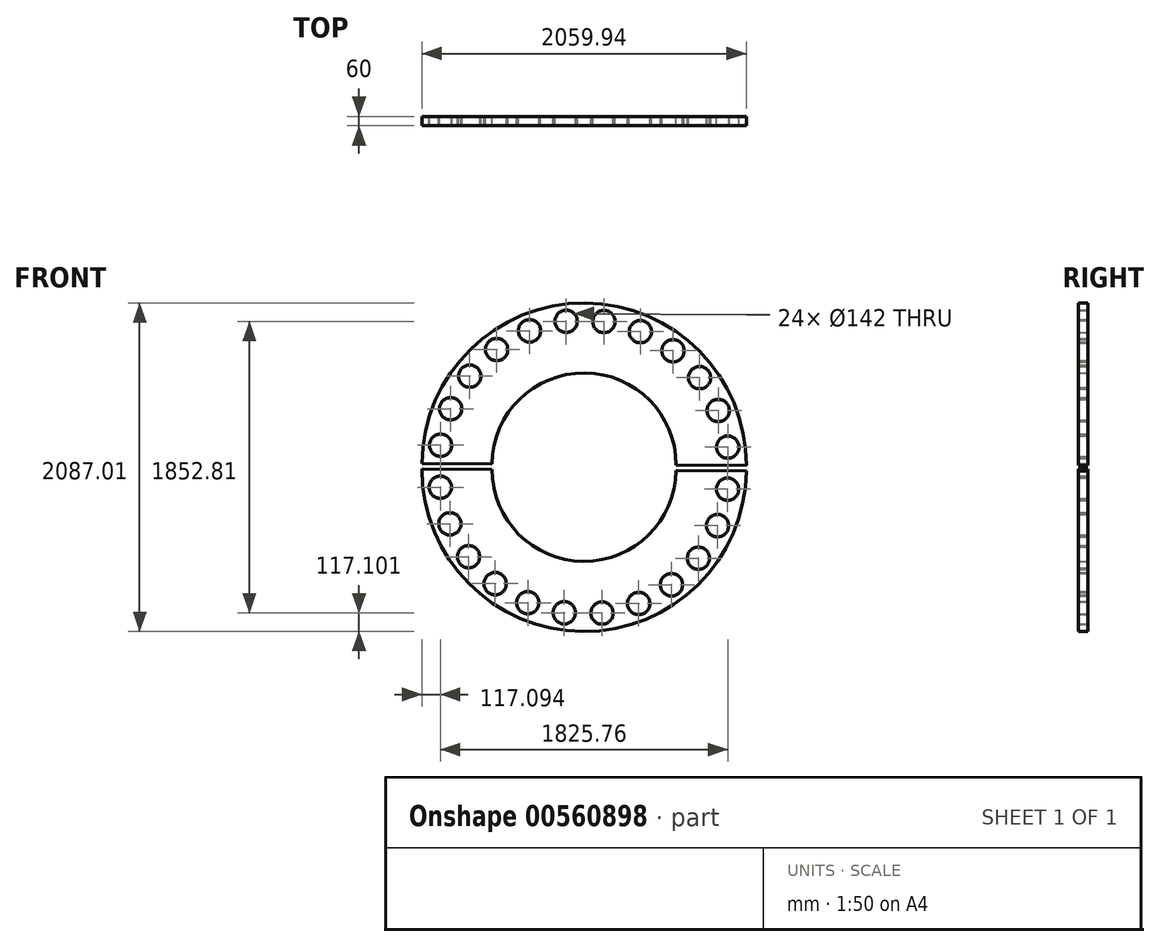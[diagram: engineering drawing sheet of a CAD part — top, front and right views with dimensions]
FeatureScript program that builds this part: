
annotation { "Feature Type Name" : "Feature", "Feature Type Description" : "" }
export const myFeature = defineFeature(function(context is Context, id is Id, definition is map)
    precondition{}
    {
        {
            var Q0;
            Q0=qCreatedBy(makeId("Front.planeOp"),FACE);
            var sketch = newSketch(context, id + "F0", { "sketchPlane" : qUnion([Q0])});
            skLineSegment(sketch, "E0", {"start": v(901.46, 10.69) * mm, "end": v(456.46, 13.63) * mm});
            skLineSegment(sketch, "E1", {"start": v(901.46, -24.31) * mm, "end": v(456.46, -21.37) * mm});
            skLineSegment(sketch, "E2", {"start": v(2071.4, 2.94) * mm, "end": v(2516.4, 0) * mm});
            skLineSegment(sketch, "E3", {"start": v(2071.4, -32.06) * mm, "end": v(2516.4, -35) * mm});
            skArc(sketch, "E4", {"start": v(456.46, 13.63) * mm, "mid": v(1493.22, 1032.8) * mm, "end": v(2516.4, 0) * mm});
            skArc(sketch, "E5", {"start": v(456.46, -21.37) * mm, "mid": v(1479.64, -1054.16) * mm, "end": v(2516.4, -35) * mm});
            skArc(sketch, "E6", {"start": v(901.46, -24.31) * mm, "mid": v(1482.59, -609.17) * mm, "end": v(2071.4, -32.06) * mm});
            skArc(sketch, "E7", {"start": v(901.46, 10.69) * mm, "mid": v(1490.28, 587.8) * mm, "end": v(2071.4, 2.94) * mm});
            skLineSegment(sketch, "E8", {"start": v(456.46, 13.63) * mm, "end": v(456.23, -21.37) * mm, "construction": true});
            skLineSegment(sketch, "E9", {"start": v(2516.4, -35) * mm, "end": v(2516.63, 0) * mm, "construction": true});
            skArc(sketch, "E10", {"start": v(566.46, 12.9) * mm, "mid": v(1492.5, 922.8) * mm, "end": v(2406.4, 0.73) * mm, "construction": true});
            skLineSegment(sketch, "E11", {"start": v(1486.4, 2.82) * mm, "end": v(575.1, 128.93) * mm, "construction": true});
            skCircle(sketch, "E12", {"center": v(575.1, 128.93) * mm, "radius": 71 * mm});
            skLineSegment(sketch, "E13", {"start": v(1486.4, 2.82) * mm, "end": v(1169.22, 4.91) * mm, "construction": true});
            skCircle(sketch, "E14.1.0", {"center": v(638.78, 360.5) * mm, "radius": 71 * mm});
            skCircle(sketch, "E14.2.0", {"center": v(760.24, 567.7) * mm, "radius": 71 * mm});
            skCircle(sketch, "E14.3.0", {"center": v(931.19, 736.4) * mm, "radius": 71 * mm});
            skCircle(sketch, "E14.4.0", {"center": v(1139.97, 855.1) * mm, "radius": 71 * mm});
            skCircle(sketch, "E14.5.0", {"center": v(1372.36, 915.72) * mm, "radius": 71 * mm});
            skCircle(sketch, "E14.6.0", {"center": v(1612.52, 914.13) * mm, "radius": 71 * mm});
            skCircle(sketch, "E14.7.0", {"center": v(1844.1, 850.44) * mm, "radius": 71 * mm});
            skCircle(sketch, "E14.8.0", {"center": v(2051.28, 728.98) * mm, "radius": 71 * mm});
            skCircle(sketch, "E14.9.0", {"center": v(2219.98, 558.03) * mm, "radius": 71 * mm});
            skCircle(sketch, "E14.10.0", {"center": v(2338.69, 349.25) * mm, "radius": 71 * mm});
            skCircle(sketch, "E14.11.0", {"center": v(2399.3, 116.86) * mm, "radius": 71 * mm});
            skLineSegment(sketch, "E14.anchor2", {"start": v(1486.4, 2.82) * mm, "end": v(2399.3, 116.86) * mm, "construction": true});
            skArc(sketch, "E15", {"start": v(566.46, -22.1) * mm, "mid": v(1480.37, -944.17) * mm, "end": v(2406.4, -34.27) * mm, "construction": true});
            skLineSegment(sketch, "E16", {"start": v(1486.46, -24.19) * mm, "end": v(2081.96, -28.13) * mm, "construction": true});
            skLineSegment(sketch, "E17", {"start": v(1486.46, -24.19) * mm, "end": v(2397.77, -150.3) * mm, "construction": true});
            skCircle(sketch, "E18", {"center": v(2397.77, -150.3) * mm, "radius": 71 * mm});
            skCircle(sketch, "E19.1.0", {"center": v(2334.08, -381.87) * mm, "radius": 71 * mm});
            skCircle(sketch, "E19.2.0", {"center": v(2212.62, -589.06) * mm, "radius": 71 * mm});
            skCircle(sketch, "E19.3.0", {"center": v(2041.68, -757.76) * mm, "radius": 71 * mm});
            skCircle(sketch, "E19.4.0", {"center": v(1832.9, -876.47) * mm, "radius": 71 * mm});
            skCircle(sketch, "E19.5.0", {"center": v(1600.5, -937.09) * mm, "radius": 71 * mm});
            skCircle(sketch, "E19.6.0", {"center": v(1360.34, -935.5) * mm, "radius": 71 * mm});
            skCircle(sketch, "E19.7.0", {"center": v(1128.77, -871.8) * mm, "radius": 71 * mm});
            skCircle(sketch, "E19.8.0", {"center": v(921.58, -750.35) * mm, "radius": 71 * mm});
            skCircle(sketch, "E19.9.0", {"center": v(752.88, -579.4) * mm, "radius": 71 * mm});
            skCircle(sketch, "E19.10.0", {"center": v(634.18, -370.62) * mm, "radius": 71 * mm});
            skCircle(sketch, "E19.11.0", {"center": v(573.55, -138.23) * mm, "radius": 71 * mm});
            skLineSegment(sketch, "E19.anchor2", {"start": v(1486.46, -24.19) * mm, "end": v(573.55, -138.23) * mm, "construction": true});
            skLineSegment(sketch, "E20", {"start": v(324.78, -138.23) * mm, "end": v(-1808.55, 249.71) * mm});
            skLineSegment(sketch, "E21", {"start": v(-1808.55, 249.71) * mm, "end": v(365.65, 411.39) * mm});
            skLineSegment(sketch, "E22", {"start": v(365.65, 411.39) * mm, "end": v(324.78, -138.23) * mm});
            skLineSegment(sketch, "E23", {"start": v(1991.2, 1056.17) * mm, "end": v(2514.38, 698.66) * mm});
            skLineSegment(sketch, "E24", {"start": v(2514.38, 698.66) * mm, "end": v(3334.02, 2259.48) * mm});
            skLineSegment(sketch, "E25", {"start": v(3334.02, 2259.48) * mm, "end": v(1991.2, 1056.17) * mm});
            skLineSegment(sketch, "E26", {"start": v(2204.96, -991.46) * mm, "end": v(2566.2, -534.66) * mm});
            skLineSegment(sketch, "E27", {"start": v(2566.2, -534.66) * mm, "end": v(3635.4, -2088.95) * mm});
            skLineSegment(sketch, "E28", {"start": v(3635.4, -2088.95) * mm, "end": v(2204.96, -991.46) * mm});
            skSolve(sketch);
        }
        {
            var Q0;
            Q0=makeQuery(id+"F0.imprint","IMPRINT",FACE,{"disambiguationData":[TD([[makeQuery(id+"F0.imprint","IMPRINT",EDGE,{"derivedFrom":sQuery(id+"F0.wireOp",EDGE,"E0")}),-1.0]])]});
            var Q1;
            Q1=makeQuery(id+"F0.imprint","IMPRINT",FACE,{"disambiguationData":[TD([[makeQuery(id+"F0.imprint","IMPRINT",EDGE,{"derivedFrom":sQuery(id+"F0.wireOp",EDGE,"E1")}),1.0]])]});
            extrude(context, id + "F1", {"entities" : qUnion([Q0, Q1]), "depth" : 60 * mm, "offsetDistance" : 25 * mm});
        }
    });
